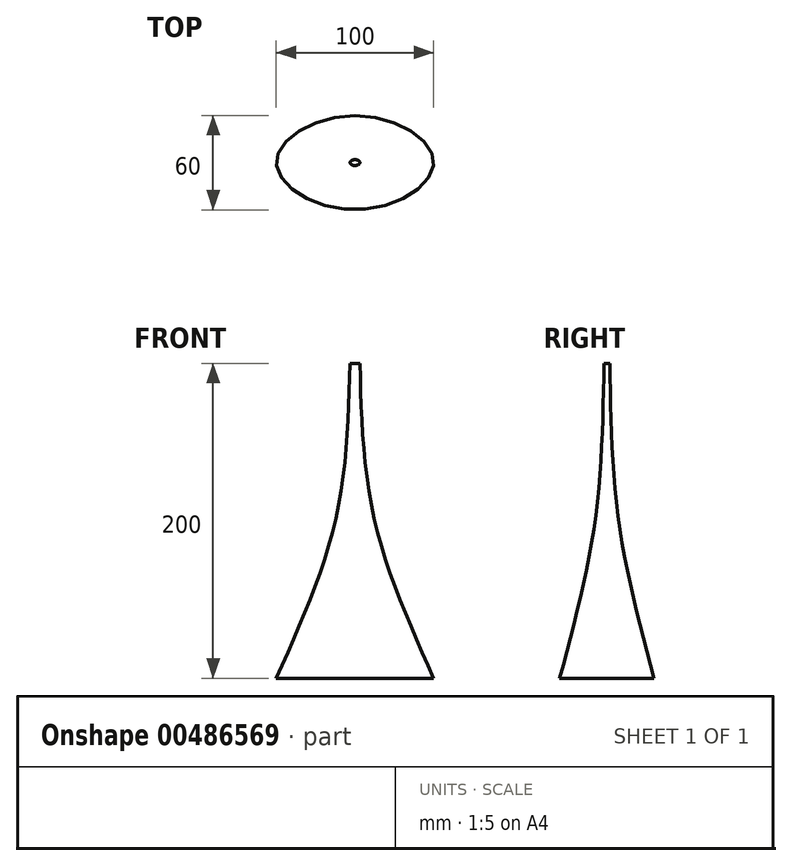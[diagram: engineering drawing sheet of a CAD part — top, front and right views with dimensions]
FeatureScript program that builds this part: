
annotation { "Feature Type Name" : "Feature", "Feature Type Description" : "" }
export const myFeature = defineFeature(function(context is Context, id is Id, definition is map)
    precondition{}
    {
        {
            var Q0;
            Q0=qCreatedBy(makeId("Top.planeOp"),FACE);
            var sketch = newSketch(context, id + "F0", { "sketchPlane" : qUnion([Q0])});
            skLineSegment(sketch, "E0", {"start": v(0, 0) * mm, "end": v(0, 30) * mm});
            skFitSpline(sketch, "E1", {"points": [v(-50, 0) * mm, v(0, 30) * mm, v(50, 0) * mm, v(0, -30) * mm, v(-50, 0) * mm]});
            skSolve(sketch);
        }
        {
            var Q0;
            Q0=qCreatedBy(makeId("Top.planeOp"),FACE);
            cPlane(context, id + "F1", {"entities" : qUnion([Q0]), "cplaneType" : CPlaneType.OFFSET, "offset" : 100 * mm, "width" : 150 * mm, "height" : 150 * mm});
        }
        {
            var Q0;
            Q0=qCreatedBy(id+"F1.planeOp",FACE);
            var sketch = newSketch(context, id + "F2", { "sketchPlane" : qUnion([Q0])});
            skLineSegment(sketch, "E2", {"start": v(0, 0) * mm, "end": v(12.5, 0) * mm});
            skFitSpline(sketch, "E3", {"points": [v(-12.5, 0) * mm, v(0, -7.5) * mm, v(12.5, 0) * mm, v(0, 7.5) * mm, v(-12.5, 0) * mm]});
            skSolve(sketch);
        }
        {
            var Q0;
            Q0=qCreatedBy(id+"F1.planeOp",FACE);
            cPlane(context, id + "F3", {"entities" : qUnion([Q0]), "cplaneType" : CPlaneType.OFFSET, "offset" : 100 * mm, "width" : 150 * mm, "height" : 150 * mm});
        }
        {
            var Q0;
            Q0=qCreatedBy(id+"F3.planeOp",FACE);
            var sketch = newSketch(context, id + "F4", { "sketchPlane" : qUnion([Q0])});
            skLineSegment(sketch, "E4", {"start": v(0, 0) * mm, "end": v(-3.12, 0) * mm});
            skFitSpline(sketch, "E5", {"points": [v(-3.12, 0) * mm, v(0, 1.88) * mm, v(3.12, 0) * mm, v(0, -1.88) * mm, v(-3.12, 0) * mm]});
            skSolve(sketch);
        }
        {
            var Q0;
            Q0=makeQuery(id+"F0.imprint","IMPRINT",FACE,{"disambiguationData":[TD([[makeQuery(id+"F0.imprint","IMPRINT",EDGE,{"derivedFrom":sQuery(id+"F0.wireOp",EDGE,"E1")}),-1.0]])]});
            var Q1;
            Q1=makeQuery(id+"F2.imprint","IMPRINT",FACE,{"disambiguationData":[TD([[makeQuery(id+"F2.imprint","IMPRINT",EDGE,{"derivedFrom":sQuery(id+"F2.wireOp",EDGE,"E3")}),1.0]])]});
            var Q2;
            Q2=makeQuery(id+"F4.imprint","IMPRINT",FACE,{"disambiguationData":[TD([[makeQuery(id+"F4.imprint","IMPRINT",EDGE,{"derivedFrom":sQuery(id+"F4.wireOp",EDGE,"E5")}),-1.0]])]});
            loft(context, id + "F5", {"sheetProfilesArray" : [{ "sheetProfileEntities" : qUnion([Q0]) }, { "sheetProfileEntities" : qUnion([Q1]) }, { "sheetProfileEntities" : qUnion([Q2]) }]});
        }
    });
